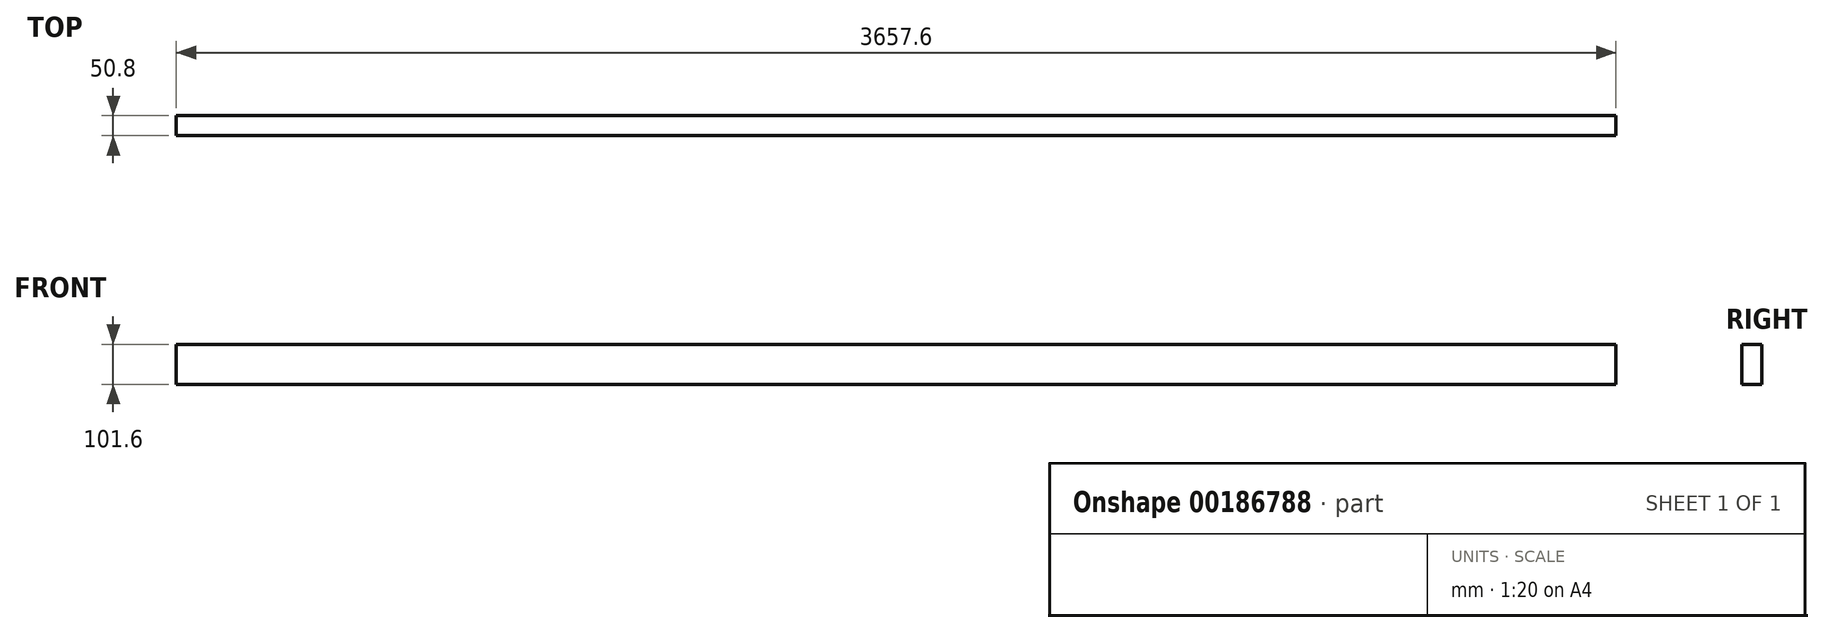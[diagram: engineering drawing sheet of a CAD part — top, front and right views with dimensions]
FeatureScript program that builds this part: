
annotation { "Feature Type Name" : "Feature", "Feature Type Description" : "" }
export const myFeature = defineFeature(function(context is Context, id is Id, definition is map)
    precondition{}
    {
        {
            var Q0;
            Q0=qCreatedBy(makeId("Right.planeOp"),FACE);
            var sketch = newSketch(context, id + "F0", { "sketchPlane" : qUnion([Q0])});
            skLineSegment(sketch, "E0.bottom", {"start": v(-25.4, 50.8) * mm, "end": v(25.4, 50.8) * mm});
            skLineSegment(sketch, "E0.top", {"start": v(-25.4, -50.8) * mm, "end": v(25.4, -50.8) * mm});
            skLineSegment(sketch, "E0.left", {"start": v(-25.4, 50.8) * mm, "end": v(-25.4, -50.8) * mm});
            skLineSegment(sketch, "E0.right", {"start": v(25.4, 50.8) * mm, "end": v(25.4, -50.8) * mm});
            skPoint(sketch, "E0.middle", {"position": v(0, 0) * mm});
            skSolve(sketch);
        }
        {
            var Q0;
            Q0 = qSketchRegion(id + "F0", true);
            extrude(context, id + "F1", {"entities" : qUnion([Q0]), "depth" : 3657.6 * mm});
        }
    });
